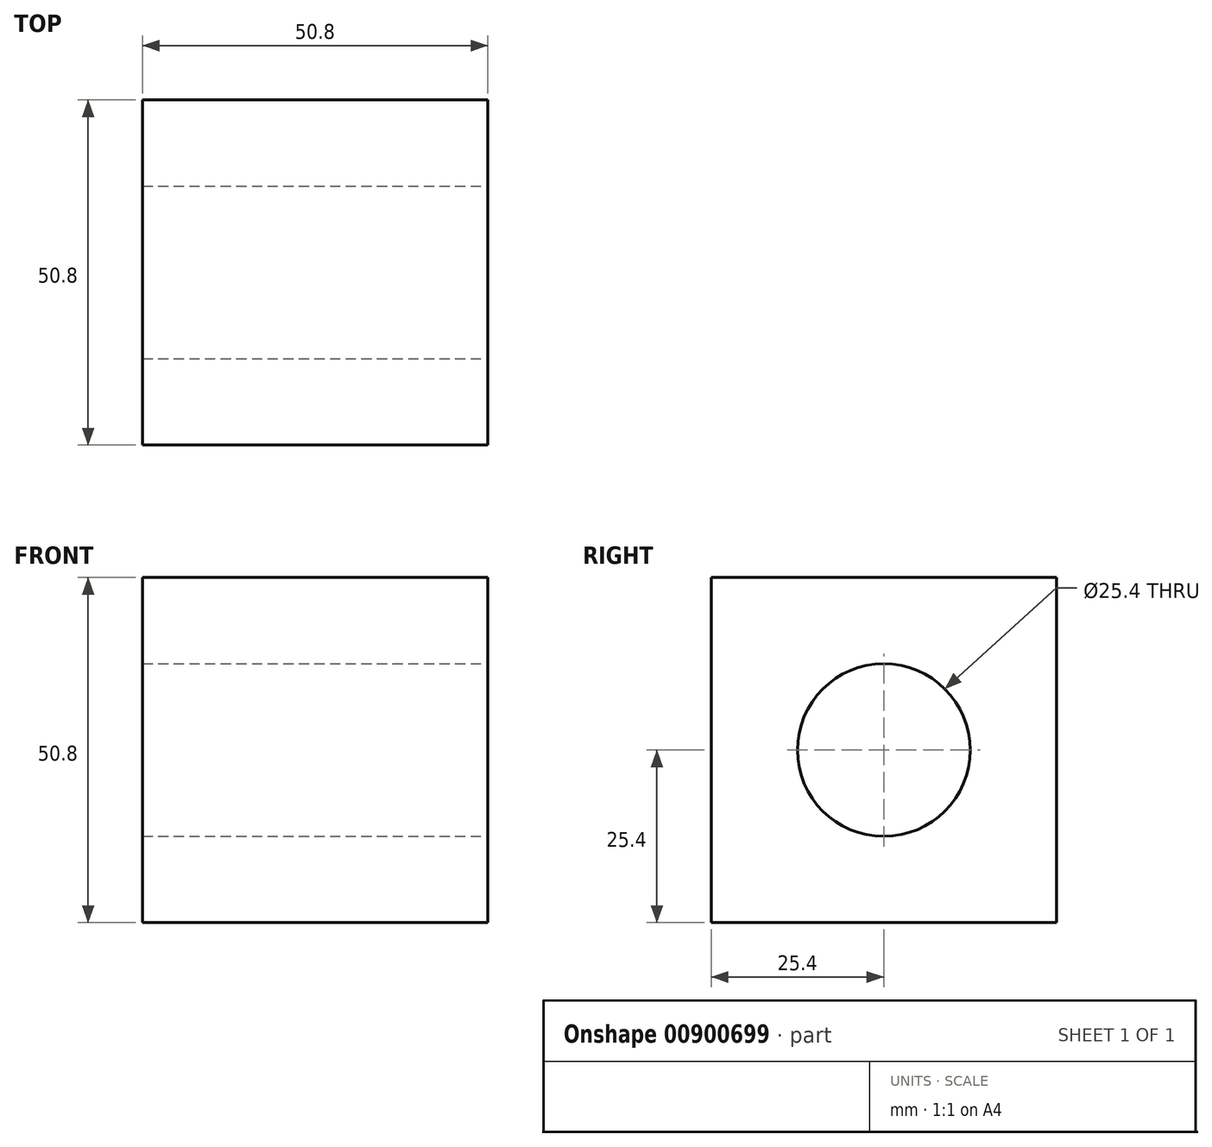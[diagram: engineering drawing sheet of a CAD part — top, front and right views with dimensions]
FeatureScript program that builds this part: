
annotation { "Feature Type Name" : "Feature", "Feature Type Description" : "" }
export const myFeature = defineFeature(function(context is Context, id is Id, definition is map)
    precondition{}
    {
        {
            var Q0;
            Q0=qCreatedBy(makeId("Top.planeOp"),FACE);
            var sketch = newSketch(context, id + "F0", { "sketchPlane" : qUnion([Q0])});
            skLineSegment(sketch, "E0.bottom", {"start": v(0, 0) * mm, "end": v(50.8, 0) * mm});
            skLineSegment(sketch, "E0.top", {"start": v(0, -50.8) * mm, "end": v(50.8, -50.8) * mm});
            skLineSegment(sketch, "E0.left", {"start": v(0, 0) * mm, "end": v(0, -50.8) * mm});
            skLineSegment(sketch, "E0.right", {"start": v(50.8, 0) * mm, "end": v(50.8, -50.8) * mm});
            skSolve(sketch);
        }
        {
            var Q0;
            Q0=makeQuery(id+"F0.imprint","IMPRINT",FACE,{"disambiguationData":[TD([[makeQuery(id+"F0.imprint","IMPRINT",EDGE,{"derivedFrom":sQuery(id+"F0.wireOp",EDGE,"E0.bottom")}),-1.0]])]});
            extrude(context, id + "F1", {"entities" : qUnion([Q0]), "depth" : 50.8 * mm, "offsetDistance" : 25.4 * mm});
        }
        {
            var Q0;
            Q0=makeQuery(id+"F1.opExtrude","SWEPT_FACE",FACE,{"disambiguationData":[OSD([sQuery(id+"F0.wireOp",EDGE,"E0.right")])]});
            var sketch = newSketch(context, id + "F2", { "sketchPlane" : qUnion([Q0])});
            skCircle(sketch, "E1", {"center": v(-25.4, 25.4) * mm, "radius": 12.7 * mm});
            skSolve(sketch);
        }
        {
            var Q0;
            Q0 = qSketchRegion(id + "F2", true);
            extrude(context, id + "F3", {"entities" : qUnion([Q0]), "operationType" : NewBodyOperationType.REMOVE, "endBound" : BoundingType.THROUGH_ALL, "oppositeDirection" : true, "depth" : 25.4 * mm, "offsetDistance" : 25.4 * mm});
        }
    });
